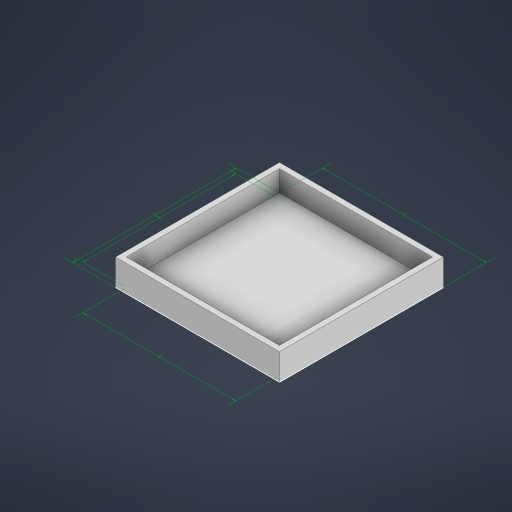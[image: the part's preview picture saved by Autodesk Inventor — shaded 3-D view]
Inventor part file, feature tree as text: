
AUTODESK INVENTOR PART (.ipt)
format: ipt  version: 2023 (Build 270158000, 158)  size: 195,072 bytes
history: native  units: mm
features: extrude x2, sketch x1
ambient origin geometry x8: Origin, YZ Plane, XZ Plane, XY Plane, X Axis, Y Axis, Z Axis, Center Point
bodies: Solid1 (feature_tree)
feature tree (3):
  sketch  "Sketch1"  dims[d0=75.0mm d1=75.0mm d2=70.0mm d3=70.0mm d4=12.0mm d5=0.0mm d6=2.5mm d7=0.0mm]
  extrude  "Extrusion1"  Depth=75.0mm
  extrude  "Extrusion2"  Depth=70.0mm
